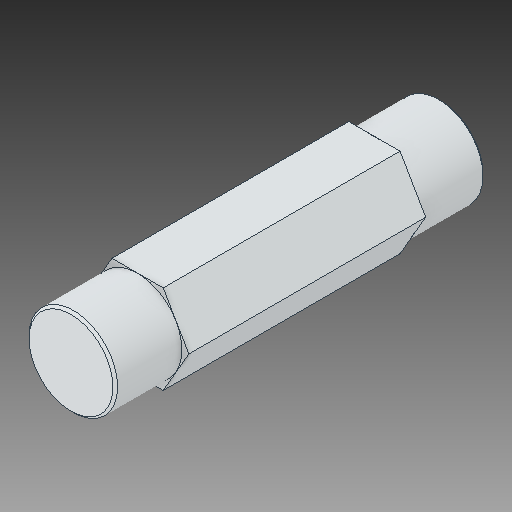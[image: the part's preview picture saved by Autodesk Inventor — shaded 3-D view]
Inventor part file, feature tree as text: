
AUTODESK INVENTOR PART (.ipt)
format: ipt  version: 2019 (Build 230136000, 136)  size: 103,424 bytes
history: native  units: in
note: dims shown in document units (in); Inventor stores cm internally (conversion verified against a paired STEP export)
features: chamfer x1
ambient origin geometry x8: Origin, YZ Plane, XZ Plane, XY Plane, X Axis, Y Axis, Z Axis, Center Point
bodies: Solid1 (feature_tree)
feature tree (1):
  chamfer  "Chamfer1"  [1 undecoded]
note: 1 required parameter value undecoded (feature->parameter linkage not recoverable at this tier; creation-order binding heuristic only, values carry confidence <= 0.55)
